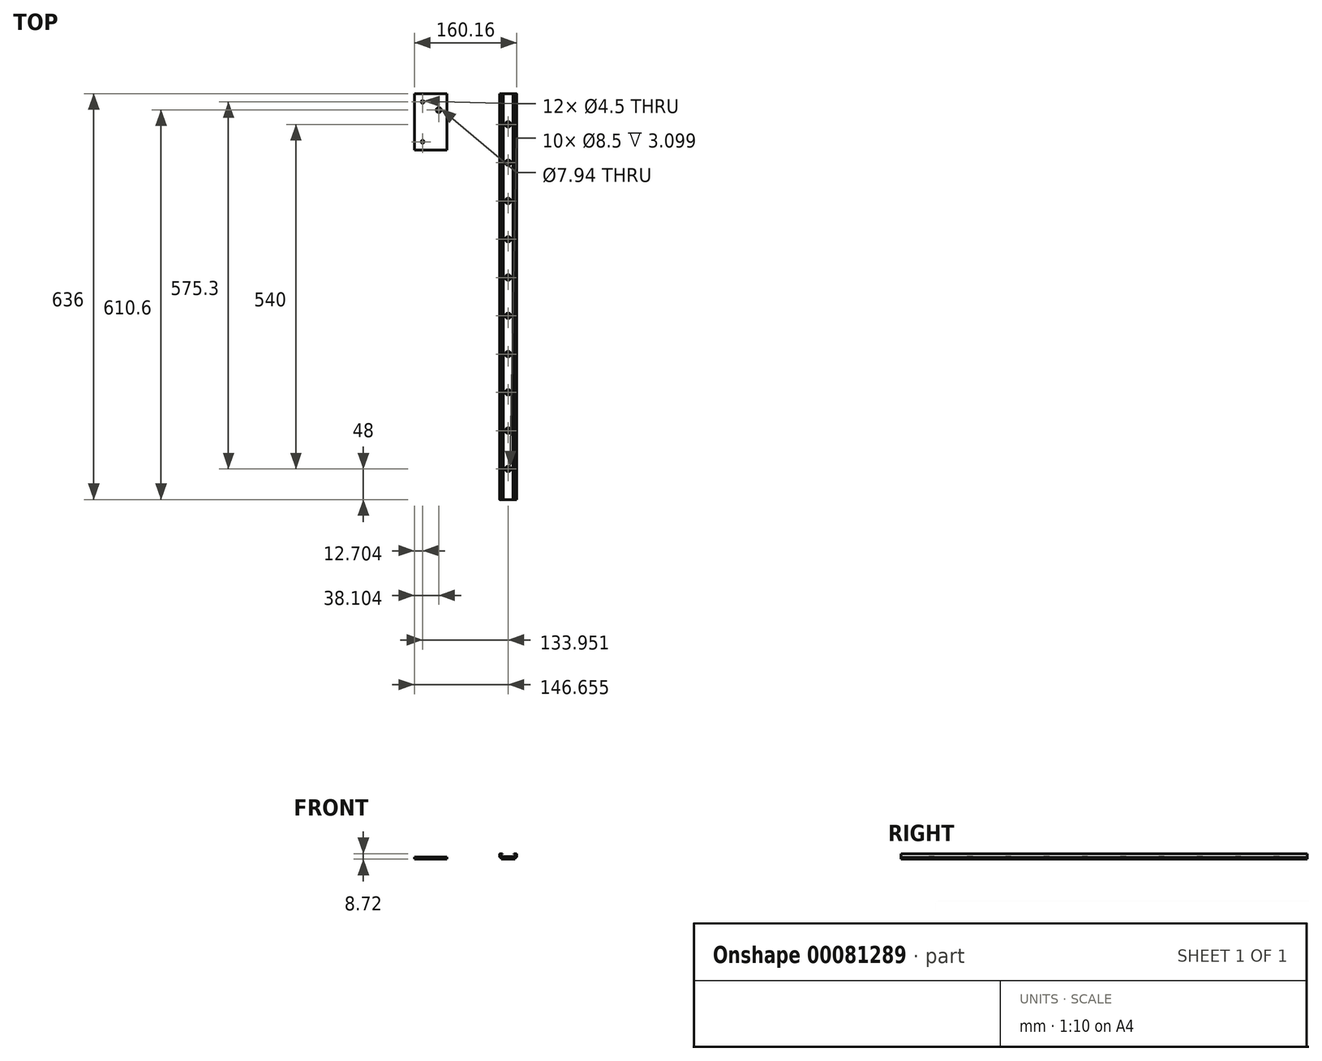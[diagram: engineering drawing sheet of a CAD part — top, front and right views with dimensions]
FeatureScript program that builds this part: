
annotation { "Feature Type Name" : "Feature", "Feature Type Description" : "" }
export const myFeature = defineFeature(function(context is Context, id is Id, definition is map)
    precondition{}
    {
        {
            var Q0;
            Q0=qCreatedBy(makeId("Front.planeOp"),FACE);
            var sketch = newSketch(context, id + "F0", { "sketchPlane" : qUnion([Q0])});
            skLineSegment(sketch, "E0", {"start": v(19.43, 4.1) * mm, "end": v(22.98, 4.1) * mm});
            skLineSegment(sketch, "E1", {"start": v(23.38, 4.1) * mm, "end": v(38.48, 4.1) * mm});
            skLineSegment(sketch, "E2", {"start": v(38.88, 4.1) * mm, "end": v(42.43, 4.1) * mm});
            skLineSegment(sketch, "E3", {"start": v(39.68, 7.6) * mm, "end": v(42.43, 7.6) * mm});
            skLineSegment(sketch, "E4", {"start": v(42.93, 7.1) * mm, "end": v(42.93, 4.6) * mm});
            skLineSegment(sketch, "E5", {"start": v(39.68, 7.6) * mm, "end": v(39.68, 8.7) * mm});
            skLineSegment(sketch, "E6", {"start": v(39.68, 8.7) * mm, "end": v(43.43, 8.7) * mm});
            skLineSegment(sketch, "E7", {"start": v(44.43, 7.7) * mm, "end": v(44.43, 4) * mm});
            skLineSegment(sketch, "E8", {"start": v(43.43, 3) * mm, "end": v(38.99, 3) * mm});
            skArc(sketch, "E9", {"start": v(43.43, 3) * mm, "mid": v(44.13, 3.3) * mm, "end": v(44.43, 4) * mm});
            skArc(sketch, "E10", {"start": v(42.43, 4.1) * mm, "mid": v(42.78, 4.25) * mm, "end": v(42.93, 4.6) * mm});
            skArc(sketch, "E11", {"start": v(42.93, 7.1) * mm, "mid": v(42.78, 7.45) * mm, "end": v(42.43, 7.6) * mm});
            skArc(sketch, "E12", {"start": v(44.43, 7.7) * mm, "mid": v(44.13, 8.4) * mm, "end": v(43.43, 8.7) * mm});
            skLineSegment(sketch, "E13", {"start": v(38.99, 3) * mm, "end": v(38.73, 3) * mm});
            skArc(sketch, "E14", {"start": v(38.73, 3) * mm, "mid": v(37.98, 2.25) * mm, "end": v(38.73, 1.5) * mm});
            skLineSegment(sketch, "E15", {"start": v(38.73, 1.5) * mm, "end": v(41.73, 1.5) * mm});
            skLineSegment(sketch, "E16", {"start": v(41.93, 1.3) * mm, "end": v(41.93, 0) * mm});
            skLineSegment(sketch, "E17", {"start": v(41.93, 0) * mm, "end": v(19.93, 0) * mm});
            skLineSegment(sketch, "E18", {"start": v(19.93, 0) * mm, "end": v(19.93, 1.3) * mm});
            skLineSegment(sketch, "E19", {"start": v(20.13, 1.5) * mm, "end": v(23.13, 1.5) * mm});
            skLineSegment(sketch, "E20", {"start": v(23.13, 3) * mm, "end": v(18.43, 3) * mm});
            skLineSegment(sketch, "E21", {"start": v(17.43, 4) * mm, "end": v(17.43, 7.7) * mm});
            skLineSegment(sketch, "E22", {"start": v(18.63, 8.7) * mm, "end": v(22.18, 8.7) * mm});
            skLineSegment(sketch, "E23", {"start": v(22.18, 8.7) * mm, "end": v(22.18, 7.6) * mm});
            skLineSegment(sketch, "E24", {"start": v(22.18, 7.6) * mm, "end": v(19.43, 7.6) * mm});
            skLineSegment(sketch, "E25", {"start": v(18.93, 7.1) * mm, "end": v(18.93, 4.6) * mm});
            skArc(sketch, "E26", {"start": v(18.63, 8.7) * mm, "mid": v(17.8, 8.48) * mm, "end": v(17.43, 7.7) * mm});
            skArc(sketch, "E27", {"start": v(19.43, 7.6) * mm, "mid": v(19.07, 7.45) * mm, "end": v(18.93, 7.1) * mm});
            skArc(sketch, "E28", {"start": v(18.93, 4.6) * mm, "mid": v(19.07, 4.25) * mm, "end": v(19.43, 4.1) * mm});
            skArc(sketch, "E29", {"start": v(22.98, 4.1) * mm, "mid": v(23.18, 3.9) * mm, "end": v(23.38, 4.1) * mm});
            skArc(sketch, "E30", {"start": v(23.13, 1.5) * mm, "mid": v(23.88, 2.25) * mm, "end": v(23.13, 3) * mm});
            skArc(sketch, "E31", {"start": v(20.13, 1.5) * mm, "mid": v(19.98, 1.44) * mm, "end": v(19.93, 1.3) * mm});
            skArc(sketch, "E32", {"start": v(38.48, 4.1) * mm, "mid": v(38.68, 3.9) * mm, "end": v(38.88, 4.1) * mm});
            skArc(sketch, "E33", {"start": v(41.93, 1.3) * mm, "mid": v(41.87, 1.44) * mm, "end": v(41.73, 1.5) * mm});
            skArc(sketch, "E34", {"start": v(17.43, 4) * mm, "mid": v(17.72, 3.3) * mm, "end": v(18.43, 3) * mm});
            skSolve(sketch);
        }
        {
            var Q0;
            Q0=makeQuery(id+"F0.imprint","IMPRINT",FACE,{"disambiguationData":[TD([[makeQuery(id+"F0.imprint","IMPRINT",EDGE,{"derivedFrom":sQuery(id+"F0.wireOp",EDGE,"E0")}),-1.0]])]});
            extrude(context, id + "F1", {"entities" : qUnion([Q0]), "depth" : 636 * mm});
        }
        {
            var Q0;
            Q0=makeQuery(id+"F1.opExtrude","SWEPT_FACE",FACE,{"disambiguationData":[OSD([sQuery(id+"F0.wireOp",EDGE,"E1")])]});
            var sketch = newSketch(context, id + "F2", { "sketchPlane" : qUnion([Q0])});
            skCircle(sketch, "E35", {"center": v(30.93, -108) * mm, "radius": 4.25 * mm});
            skCircle(sketch, "E36", {"center": v(30.93, -48) * mm, "radius": 4.25 * mm});
            skCircle(sketch, "E37", {"center": v(30.93, -108) * mm, "radius": 2.25 * mm});
            skCircle(sketch, "E38", {"center": v(30.93, -48) * mm, "radius": 2.25 * mm});
            skCircle(sketch, "E39", {"center": v(30.93, -168) * mm, "radius": 4.25 * mm});
            skCircle(sketch, "E40", {"center": v(30.93, -168) * mm, "radius": 2.25 * mm});
            skCircle(sketch, "E41", {"center": v(30.93, -228) * mm, "radius": 4.25 * mm});
            skCircle(sketch, "E42", {"center": v(30.93, -228) * mm, "radius": 2.25 * mm});
            skCircle(sketch, "E43", {"center": v(30.93, -288) * mm, "radius": 4.25 * mm});
            skCircle(sketch, "E44", {"center": v(30.93, -288) * mm, "radius": 2.25 * mm});
            skCircle(sketch, "E45", {"center": v(30.93, -348) * mm, "radius": 4.25 * mm});
            skCircle(sketch, "E46", {"center": v(30.93, -348) * mm, "radius": 2.25 * mm});
            skCircle(sketch, "E47", {"center": v(30.93, -408) * mm, "radius": 4.25 * mm});
            skCircle(sketch, "E48", {"center": v(30.93, -408) * mm, "radius": 2.25 * mm});
            skCircle(sketch, "E49", {"center": v(30.93, -468) * mm, "radius": 4.25 * mm});
            skCircle(sketch, "E50", {"center": v(30.93, -468) * mm, "radius": 2.25 * mm});
            skCircle(sketch, "E51", {"center": v(30.93, -528) * mm, "radius": 4.25 * mm});
            skCircle(sketch, "E52", {"center": v(30.93, -528) * mm, "radius": 2.25 * mm});
            skCircle(sketch, "E53", {"center": v(30.93, -588) * mm, "radius": 4.25 * mm});
            skCircle(sketch, "E54", {"center": v(30.93, -588) * mm, "radius": 2.25 * mm});
            skSolve(sketch);
        }
        {
            var Q0;
            Q0=makeQuery(id+"F2.imprint","IMPRINT",FACE,{"disambiguationData":[TD([[makeQuery(id+"F2.imprint","IMPRINT",EDGE,{"derivedFrom":sQuery(id+"F2.wireOp",EDGE,"E38")}),1.0]])]});
            var Q1;
            Q1=makeQuery(id+"F2.imprint","IMPRINT",FACE,{"disambiguationData":[TD([[makeQuery(id+"F2.imprint","IMPRINT",EDGE,{"derivedFrom":sQuery(id+"F2.wireOp",EDGE,"E37")}),1.0]])]});
            var Q2;
            Q2=makeQuery(id+"F2.imprint","IMPRINT",FACE,{"disambiguationData":[TD([[makeQuery(id+"F2.imprint","IMPRINT",EDGE,{"derivedFrom":sQuery(id+"F2.wireOp",EDGE,"E40")}),1.0]])]});
            var Q3;
            Q3=makeQuery(id+"F2.imprint","IMPRINT",FACE,{"disambiguationData":[TD([[makeQuery(id+"F2.imprint","IMPRINT",EDGE,{"derivedFrom":sQuery(id+"F2.wireOp",EDGE,"E42")}),1.0]])]});
            var Q4;
            Q4=makeQuery(id+"F2.imprint","IMPRINT",FACE,{"disambiguationData":[TD([[makeQuery(id+"F2.imprint","IMPRINT",EDGE,{"derivedFrom":sQuery(id+"F2.wireOp",EDGE,"E44")}),1.0]])]});
            var Q5;
            Q5=makeQuery(id+"F2.imprint","IMPRINT",FACE,{"disambiguationData":[TD([[makeQuery(id+"F2.imprint","IMPRINT",EDGE,{"derivedFrom":sQuery(id+"F2.wireOp",EDGE,"E46")}),1.0]])]});
            var Q6;
            Q6=makeQuery(id+"F2.imprint","IMPRINT",FACE,{"disambiguationData":[TD([[makeQuery(id+"F2.imprint","IMPRINT",EDGE,{"derivedFrom":sQuery(id+"F2.wireOp",EDGE,"E48")}),1.0]])]});
            var Q7;
            Q7=makeQuery(id+"F2.imprint","IMPRINT",FACE,{"disambiguationData":[TD([[makeQuery(id+"F2.imprint","IMPRINT",EDGE,{"derivedFrom":sQuery(id+"F2.wireOp",EDGE,"E50")}),1.0]])]});
            var Q8;
            Q8=makeQuery(id+"F2.imprint","IMPRINT",FACE,{"disambiguationData":[TD([[makeQuery(id+"F2.imprint","IMPRINT",EDGE,{"derivedFrom":sQuery(id+"F2.wireOp",EDGE,"E52")}),1.0]])]});
            var Q9;
            Q9=makeQuery(id+"F2.imprint","IMPRINT",FACE,{"disambiguationData":[TD([[makeQuery(id+"F2.imprint","IMPRINT",EDGE,{"derivedFrom":sQuery(id+"F2.wireOp",EDGE,"E54")}),1.0]])]});
            var Q10;
            Q10=makeQuery(id+"F2.imprint","IMPRINT",FACE,{"disambiguationData":[TD([[makeQuery(id+"F2.imprint","IMPRINT",EDGE,{"derivedFrom":sQuery(id+"F2.wireOp",EDGE,"539903d2-8d8b-45e9-85ca-9de845f189c4")}),1.0]])]});
            var Q11;
            Q11=makeQuery(id+"F2.imprint","IMPRINT",FACE,{"disambiguationData":[TD([[makeQuery(id+"F2.imprint","IMPRINT",EDGE,{"derivedFrom":sQuery(id+"F2.wireOp",EDGE,"edbae3d4-dce5-4c6e-a04b-cea7b68aa30f")}),1.0]])]});
            extrude(context, id + "F3", {"entities" : qUnion([Q0, Q1, Q2, Q3, Q4, Q5, Q6, Q7, Q8, Q9, Q10, Q11]), "operationType" : NewBodyOperationType.REMOVE, "endBound" : BoundingType.THROUGH_ALL, "oppositeDirection" : true, "depth" : 25.4 * mm});
        }
        {
            var Q0;
            Q0 = qSketchRegion(id + "F2", true);
            var Q1;
            Q1=sQuery(id+"F2.wireOp",EDGE,"E36");
            extrude(context, id + "F4", {"entities" : qUnion([Q0]), "operationType" : NewBodyOperationType.REMOVE, "surfaceEntities" : qUnion([Q1]), "oppositeDirection" : true, "depth" : 3.1 * mm});
        }
        {
            var Q0;
            Q0=qCreatedBy(makeId("Top.planeOp"),FACE);
            var sketch = newSketch(context, id + "F5", { "sketchPlane" : qUnion([Q0])});
            skLineSegment(sketch, "E55.bottom", {"start": v(-115.73, 0) * mm, "end": v(-64.93, 0) * mm});
            skLineSegment(sketch, "E55.top", {"start": v(-115.73, -87.94) * mm, "end": v(-64.93, -87.94) * mm});
            skLineSegment(sketch, "E55.left", {"start": v(-115.73, 0) * mm, "end": v(-115.73, -87.94) * mm});
            skLineSegment(sketch, "E55.right", {"start": v(-64.93, 0) * mm, "end": v(-64.93, -87.94) * mm});
            skCircle(sketch, "E56", {"center": v(-103.03, -12.7) * mm, "radius": 2.25 * mm});
            skCircle(sketch, "E57", {"center": v(-103.03, -75.24) * mm, "radius": 2.25 * mm});
            skCircle(sketch, "E58", {"center": v(-77.63, -25.4) * mm, "radius": 3.97 * mm});
            skSolve(sketch);
        }
        {
            var Q0;
            Q0 = qSketchRegion(id + "F5", true);
            extrude(context, id + "F6", {"entities" : qUnion([Q0]), "depth" : 3.17 * mm});
        }
    });
